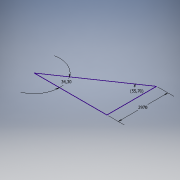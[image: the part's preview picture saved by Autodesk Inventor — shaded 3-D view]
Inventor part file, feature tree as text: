
AUTODESK INVENTOR PART (.ipt)
format: ipt  version: 2018 (Build 220112000, 112)  size: 87,552 bytes
history: native  units: mm
features: sketch x1
ambient origin geometry x8: Origin, YZ Plane, XZ Plane, XY Plane, X Axis, Y Axis, Z Axis, Center Point
feature tree (1):
  sketch  "Sketch1"  dims[d0=2970.0mm d1=5.986479mm d2=9.721484mm]
